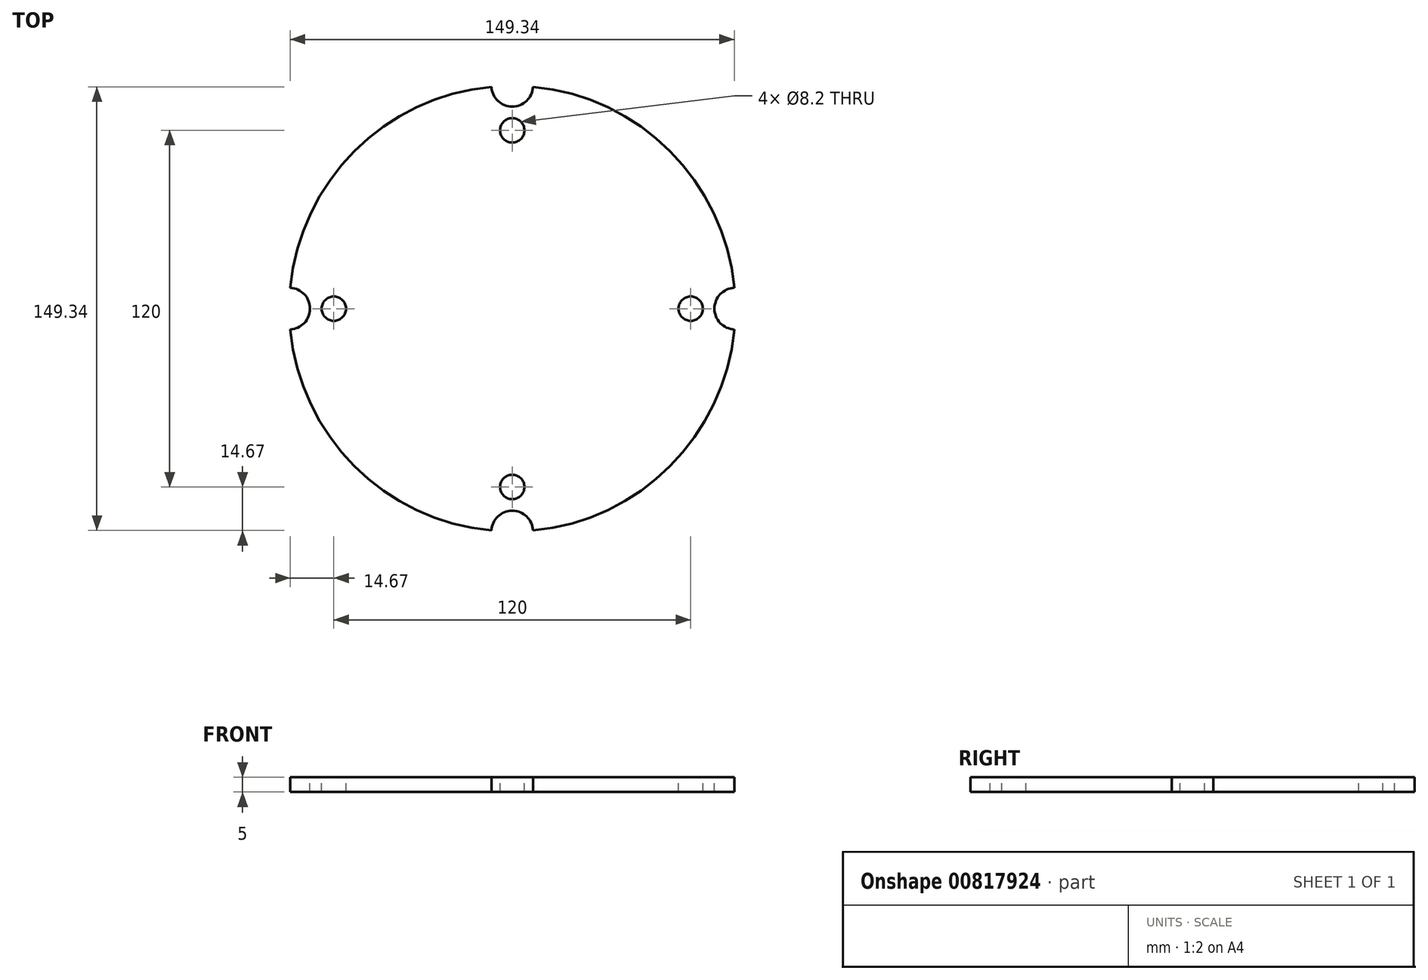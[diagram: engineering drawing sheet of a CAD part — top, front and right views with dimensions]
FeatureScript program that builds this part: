
annotation { "Feature Type Name" : "Feature", "Feature Type Description" : "" }
export const myFeature = defineFeature(function(context is Context, id is Id, definition is map)
    precondition{}
    {
        {
            var Q0;
            Q0=qCreatedBy(makeId("Top.planeOp"),FACE);
            var sketch = newSketch(context, id + "F0", { "sketchPlane" : qUnion([Q0])});
            skCircle(sketch, "E0", {"center": v(0, 0) * mm, "radius": 75 * mm});
            skSolve(sketch);
        }
        {
            var Q0;
            Q0 = qSketchRegion(id + "F0", true);
            extrude(context, id + "F1", {"entities" : qUnion([Q0]), "depth" : 5 * mm, "offsetDistance" : 25 * mm});
        }
        {
            var Q0;
            Q0=makeQuery(id+"F1.opExtrude","CAP_FACE",FACE,{"disambiguationData":[OSD([sQuery(id+"F0.wireOp",EDGE,"E0")])],"isStart":false});
            var sketch = newSketch(context, id + "F2", { "sketchPlane" : qUnion([Q0])});
            skPoint(sketch, "E1.middle", {"position": v(0, 0) * mm});
            skCircle(sketch, "E2", {"center": v(0, 60) * mm, "radius": 4.1 * mm});
            skCircle(sketch, "E3", {"center": v(60, 0) * mm, "radius": 4.1 * mm});
            skCircle(sketch, "E4", {"center": v(0, -60) * mm, "radius": 4.1 * mm});
            skCircle(sketch, "E5", {"center": v(-60, 0) * mm, "radius": 4.1 * mm});
            skArc(sketch, "E6", {"start": v(74.67, 7) * mm, "mid": v(68, 0) * mm, "end": v(74.67, -7) * mm});
            skArc(sketch, "E7", {"start": v(7, 74.67) * mm, "mid": v(0, 68) * mm, "end": v(-7, 74.67) * mm});
            skArc(sketch, "E8", {"start": v(-74.67, 7) * mm, "mid": v(-68, 0) * mm, "end": v(-74.67, -7) * mm});
            skArc(sketch, "E9", {"start": v(-7, -74.67) * mm, "mid": v(0, -68) * mm, "end": v(7, -74.67) * mm});
            skArc(sketch, "E10", {"start": v(-74.67, 7) * mm, "mid": v(-75, 0) * mm, "end": v(-74.67, -7) * mm});
            skArc(sketch, "E11", {"start": v(-7, -74.67) * mm, "mid": v(0, -75) * mm, "end": v(7, -74.67) * mm});
            skArc(sketch, "E12", {"start": v(74.67, -7) * mm, "mid": v(75, 0) * mm, "end": v(74.67, 7) * mm});
            skArc(sketch, "E13", {"start": v(7, 74.67) * mm, "mid": v(0, 75) * mm, "end": v(-7, 74.67) * mm});
            skSolve(sketch);
        }
        {
            var Q0;
            Q0 = qSketchRegion(id + "F2", true);
            var Q1;
            Q1=makeQuery(id+"F1.opExtrude","CAP_FACE",FACE,{"disambiguationData":[OSD([sQuery(id+"F0.wireOp",EDGE,"E0")])],"isStart":true});
            extrude(context, id + "F3", {"entities" : qUnion([Q0]), "operationType" : NewBodyOperationType.REMOVE, "endBound" : BoundingType.UP_TO_SURFACE, "oppositeDirection" : true, "depth" : 25 * mm, "endBoundEntityFace" : qUnion([Q1]), "offsetDistance" : 25 * mm});
        }
    });
